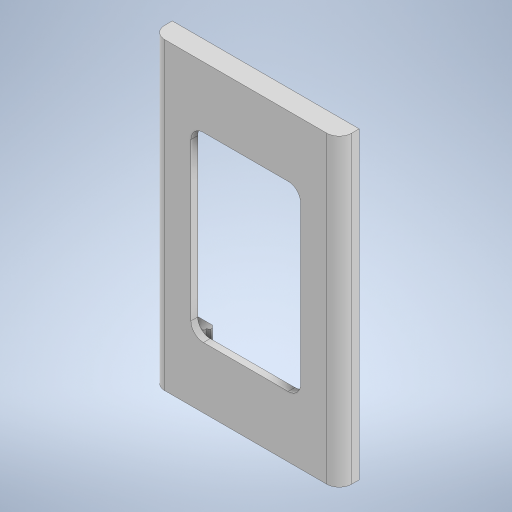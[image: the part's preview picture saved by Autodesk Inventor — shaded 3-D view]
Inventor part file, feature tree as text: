
AUTODESK INVENTOR PART (.ipt)
format: ipt  version: 2023 (Build 270158000, 158)  size: 360,960 bytes
history: native  units: mm
features: extrude x4, sketch x4, fillet x3, other x2, chamfer x2, mirror x2, shell x1
ambient origin geometry x8: Origin, YZ Plane, XZ Plane, XY Plane, X Axis, Y Axis, Z Axis, Center Point
bodies: Body1 (feature_tree)
feature tree (18):
  other  "솔리드1"
  extrude  "돌출1"  Depth=75.0mm
  fillet  "모깎기1"  Radius=122.0mm
  shell  "쉘1"  Thickness=44.0mm
  extrude  "돌출2"  Depth=73.0mm
  extrude  "돌출3"  Depth=8.0mm TaperAngle=0.0deg
  chamfer  "모따기1"  Distance=5.0mm
  extrude  "돌출4"  Depth=1.7mm
  mirror  "미러1"
  mirror  "미러2"
  sketch  "스케치5"
  fillet  "모깎기8"  Radius=8.0mm
  chamfer  "모따기3"  Distance=36.85mm
  other  "두껍게 하기2"
  fillet  "모깎기9"  Radius=6.9mm
  sketch  "스케치1"
  sketch  "스케치2"
  sketch  "스케치3"
